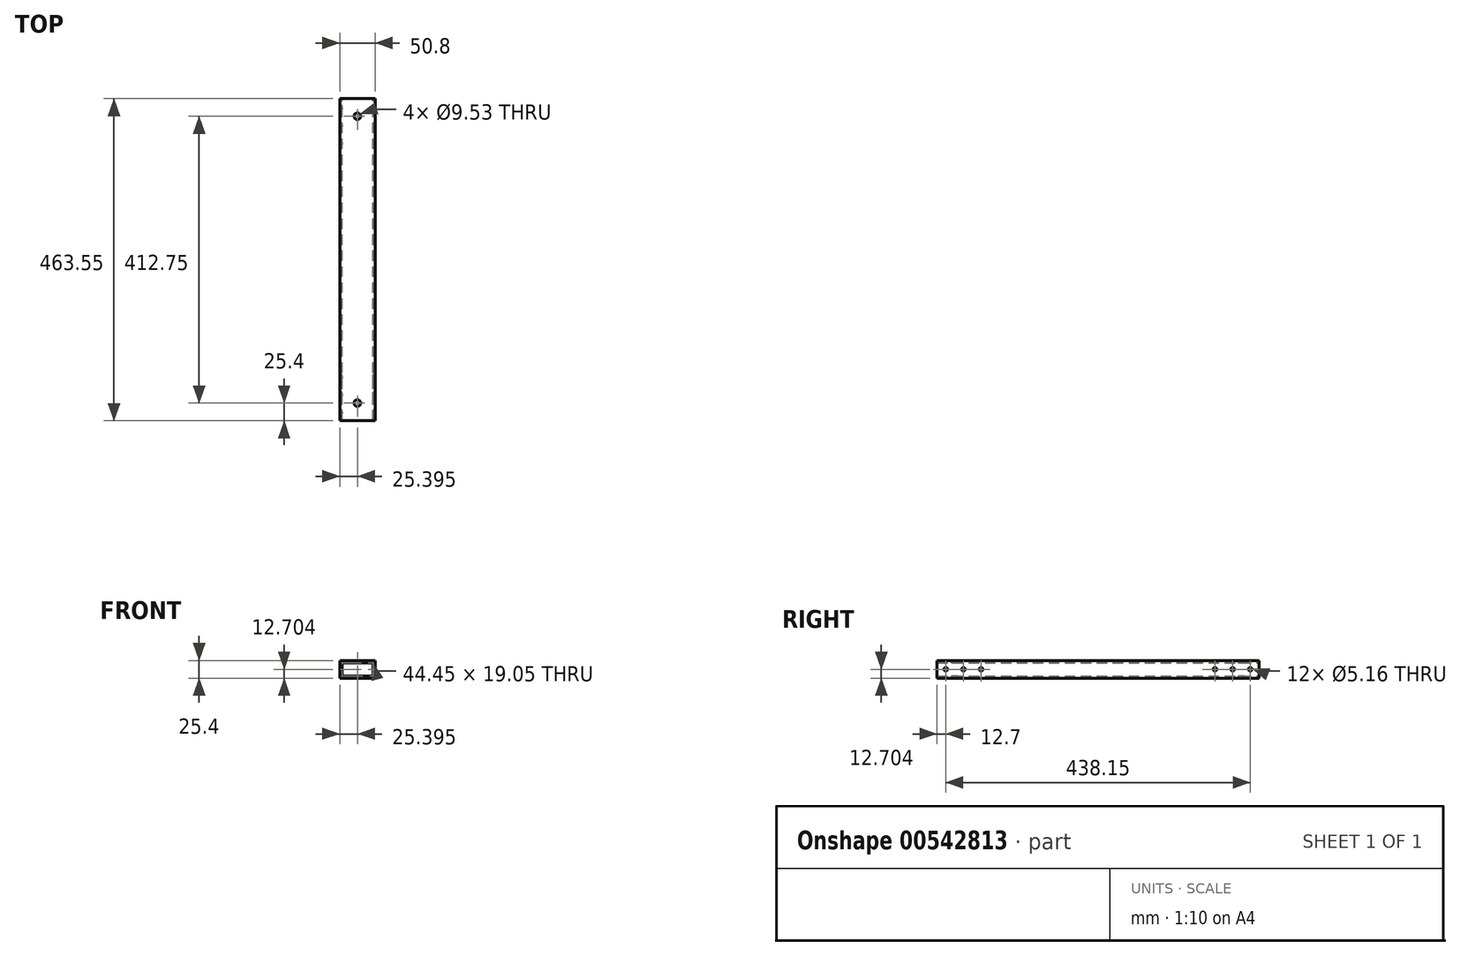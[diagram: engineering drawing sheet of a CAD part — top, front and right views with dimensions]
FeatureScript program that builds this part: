
annotation { "Feature Type Name" : "Feature", "Feature Type Description" : "" }
export const myFeature = defineFeature(function(context is Context, id is Id, definition is map)
    precondition{}
    {
        {
            var Q0;
            Q0=qCreatedBy(makeId("Front.planeOp"),FACE);
            var sketch = newSketch(context, id + "F0", { "sketchPlane" : qUnion([Q0])});
            skLineSegment(sketch, "E0.bottom", {"start": v(-31.97, 16.3) * mm, "end": v(18.83, 16.3) * mm});
            skLineSegment(sketch, "E0.top", {"start": v(-31.97, -9.1) * mm, "end": v(18.83, -9.1) * mm});
            skLineSegment(sketch, "E0.left", {"start": v(-31.97, 16.3) * mm, "end": v(-31.97, -9.1) * mm});
            skLineSegment(sketch, "E0.right", {"start": v(18.83, 16.3) * mm, "end": v(18.83, -9.1) * mm});
            skLineSegment(sketch, "E1.bottom", {"start": v(-28.8, 13.12) * mm, "end": v(15.65, 13.12) * mm});
            skLineSegment(sketch, "E1.top", {"start": v(-28.8, -5.93) * mm, "end": v(15.65, -5.93) * mm});
            skLineSegment(sketch, "E1.left", {"start": v(-28.8, 13.12) * mm, "end": v(-28.8, -5.93) * mm});
            skLineSegment(sketch, "E1.right", {"start": v(15.65, 13.12) * mm, "end": v(15.65, -5.93) * mm});
            skSolve(sketch);
        }
        {
            var Q0;
            Q0=makeQuery(id+"F0.imprint","IMPRINT",FACE,{"disambiguationData":[TD([[makeQuery(id+"F0.imprint","IMPRINT",EDGE,{"derivedFrom":sQuery(id+"F0.wireOp",EDGE,"E0.bottom")}),-1.0]])]});
            extrude(context, id + "F1", {"entities" : qUnion([Q0]), "depth" : 463.55 * mm});
        }
        {
            var Q0;
            Q0=makeQuery(id+"F1.opExtrude","SWEPT_FACE",FACE,{"disambiguationData":[OSD([sQuery(id+"F0.wireOp",EDGE,"E0.left")])]});
            var sketch = newSketch(context, id + "F2", { "sketchPlane" : qUnion([Q0])});
            skCircle(sketch, "E2", {"center": v(450.85, 3.6) * mm, "radius": 2.58 * mm});
            skPoint(sketch, "E2.centerSnap0", {"position": v(463.55, 3.6) * mm});
            skCircle(sketch, "E3", {"center": v(425.45, 3.6) * mm, "radius": 2.58 * mm});
            skCircle(sketch, "E4", {"center": v(400.05, 3.6) * mm, "radius": 2.58 * mm});
            skCircle(sketch, "E5", {"center": v(12.7, 3.6) * mm, "radius": 2.58 * mm});
            skPoint(sketch, "E5.centerSnap0", {"position": v(0, 3.6) * mm});
            skCircle(sketch, "E6", {"center": v(38.1, 3.6) * mm, "radius": 2.58 * mm});
            skCircle(sketch, "E7", {"center": v(63.5, 3.6) * mm, "radius": 2.58 * mm});
            skSolve(sketch);
        }
        {
            var Q0;
            Q0=makeQuery(id+"F2.imprint","IMPRINT",FACE,{"disambiguationData":[TD([[makeQuery(id+"F2.imprint","IMPRINT",EDGE,{"derivedFrom":sQuery(id+"F2.wireOp",EDGE,"E5")}),1.0]])]});
            var Q1;
            Q1=makeQuery(id+"F2.imprint","IMPRINT",FACE,{"disambiguationData":[TD([[makeQuery(id+"F2.imprint","IMPRINT",EDGE,{"derivedFrom":sQuery(id+"F2.wireOp",EDGE,"E6")}),1.0]])]});
            var Q2;
            Q2=makeQuery(id+"F2.imprint","IMPRINT",FACE,{"disambiguationData":[TD([[makeQuery(id+"F2.imprint","IMPRINT",EDGE,{"derivedFrom":sQuery(id+"F2.wireOp",EDGE,"E7")}),1.0]])]});
            var Q3;
            Q3=makeQuery(id+"F2.imprint","IMPRINT",FACE,{"disambiguationData":[TD([[makeQuery(id+"F2.imprint","IMPRINT",EDGE,{"derivedFrom":sQuery(id+"F2.wireOp",EDGE,"E4")}),1.0]])]});
            var Q4;
            Q4=makeQuery(id+"F2.imprint","IMPRINT",FACE,{"disambiguationData":[TD([[makeQuery(id+"F2.imprint","IMPRINT",EDGE,{"derivedFrom":sQuery(id+"F2.wireOp",EDGE,"E3")}),1.0]])]});
            var Q5;
            Q5=makeQuery(id+"F2.imprint","IMPRINT",FACE,{"disambiguationData":[TD([[makeQuery(id+"F2.imprint","IMPRINT",EDGE,{"derivedFrom":sQuery(id+"F2.wireOp",EDGE,"E2")}),1.0]])]});
            extrude(context, id + "F3", {"entities" : qUnion([Q0, Q1, Q2, Q3, Q4, Q5]), "operationType" : NewBodyOperationType.REMOVE, "endBound" : BoundingType.THROUGH_ALL, "oppositeDirection" : true, "depth" : 25.4 * mm, "offsetDistance" : 25.4 * mm});
        }
        {
            var Q0;
            Q0=makeQuery(id+"F1.opExtrude","SWEPT_FACE",FACE,{"disambiguationData":[OSD([sQuery(id+"F0.wireOp",EDGE,"E0.bottom")])]});
            var sketch = newSketch(context, id + "F4", { "sketchPlane" : qUnion([Q0])});
            skCircle(sketch, "E8", {"center": v(-6.57, -25.4) * mm, "radius": 4.76 * mm});
            skPoint(sketch, "E8.centerSnap0", {"position": v(-6.57, 0) * mm});
            skCircle(sketch, "E9", {"center": v(-6.57, -438.15) * mm, "radius": 4.76 * mm});
            skPoint(sketch, "E9.centerSnap0", {"position": v(-6.57, -463.55) * mm});
            skSolve(sketch);
        }
        {
            var Q0;
            Q0=makeQuery(id+"F4.imprint","IMPRINT",FACE,{"disambiguationData":[TD([[makeQuery(id+"F4.imprint","IMPRINT",EDGE,{"derivedFrom":sQuery(id+"F4.wireOp",EDGE,"E9")}),1.0]])]});
            var Q1;
            Q1=makeQuery(id+"F4.imprint","IMPRINT",FACE,{"disambiguationData":[TD([[makeQuery(id+"F4.imprint","IMPRINT",EDGE,{"derivedFrom":sQuery(id+"F4.wireOp",EDGE,"E8")}),1.0]])]});
            extrude(context, id + "F5", {"entities" : qUnion([Q0, Q1]), "operationType" : NewBodyOperationType.REMOVE, "endBound" : BoundingType.THROUGH_ALL, "oppositeDirection" : true, "depth" : 25.4 * mm, "offsetDistance" : 25.4 * mm});
        }
    });
